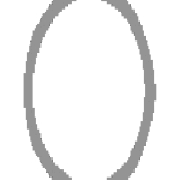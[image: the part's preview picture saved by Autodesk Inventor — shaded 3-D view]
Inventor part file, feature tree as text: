
AUTODESK INVENTOR PART (.ipt)
format: ipt  version: 2021 (Build 250183000, 183)  size: 109,568 bytes
history: native  units: in
note: dims shown in document units (in); Inventor stores cm internally (conversion verified against a paired STEP export)
features: other x4, sketch x3, plane x1
ambient origin geometry x8: Origin, YZ Plane, XZ Plane, XY Plane, X Axis, Y Axis, Z Axis, Center Point
bodies: Solid1 (feature_tree), Body (feature_tree)
feature tree (8):
  other  "Driven Length"
  other  "Frame Generator"
  other  "Start Plane"
  other  "End Plane"
  sketch  "Sketch"  dims[d2=23.8537in d4=-0.0in d5=23.8537in d6=0.12in d7=0.0in d10=90.0deg d9=23.8537in]
  sketch  "Sketch4"  dims[d0=1.0in]
  plane  "Work Plane4"
  sketch  "Sketch5"  dims[d1=0.065in]
